# Revit family: SP4250_EUR_REVIT
name_source: partatom
category: Mechanical Equipment
revit_build: Autodesk Revit 2014 (Build: 20130215_1615(x64)
units: mm (PartAtom-declared; Revit-internal decimal feet)

## types (1)
- Standard
    Connector_10_Diameter = 0' - 0"
    Connector_11_Diameter = 0' - 0"
    Connector_14_Diameter = 0' - 0"
    Connector_15_Diameter = 0' - 0"
    Connector_16_Diameter = 0' - 0"
    Connector_17_Diameter = 0' - 0"
    Connector_18_Diameter = 0' - 0"
    Description = Electric Resistive Humidifier
    Design Status = 1
    Manufacturer = Neptronic
    Model = SKE90, SKE100, SKE110, SKE120
    Part Number = SP4250_REVIT
    URL = www.neptronic.com
    d155 = 0' - 0 1/2"
    d157 = 0' - 0 1/2"
    d159 = 0' - 0 1/2"
    d161 = 0' - 0 1/2"
    d163 = 0' - 1 7/16"
    d165 = 0' - 1 7/16"
    d167 = 0' - 0 1/2"
    d169 = 0' - 0 1/2"
    d171 = 0' - 0 1/2"
    d173 = 0' - 0 1/2"
    d175 = 0' - 0 1/2"
    d177 = 0' - 5 1/2"
    d179 = 2' - 8 31/32"
    d185 = 0' - 0"

## geometry (parser evidence)
native form markers: Sweep x1
no freeform markers — native parametric forms only
